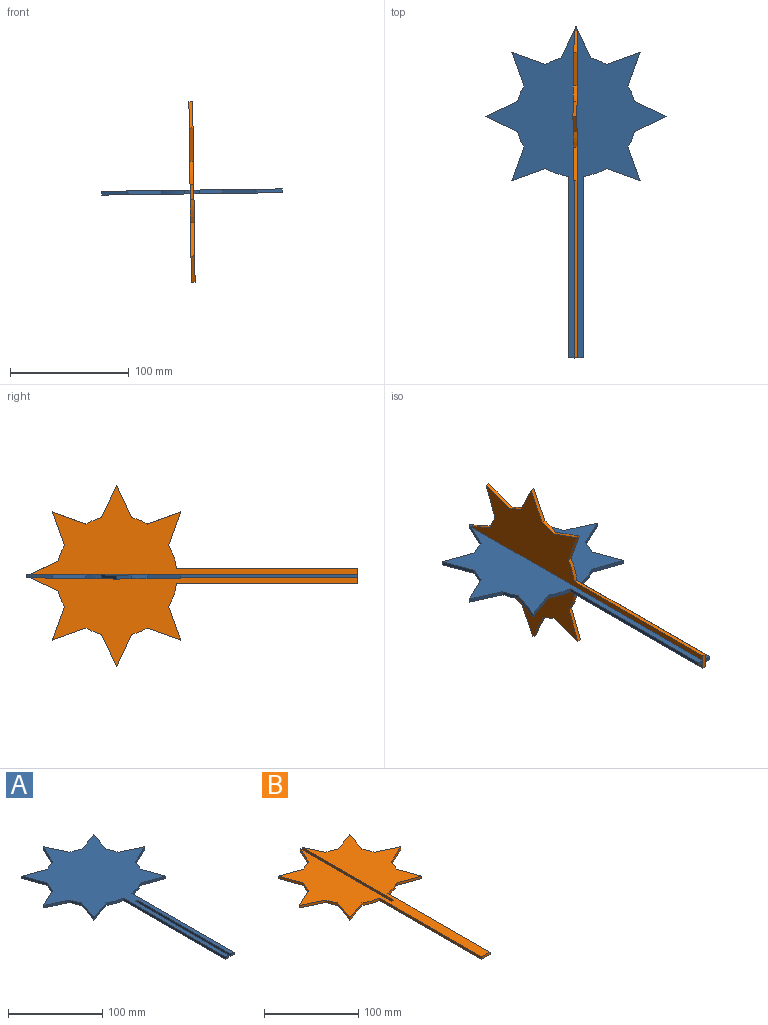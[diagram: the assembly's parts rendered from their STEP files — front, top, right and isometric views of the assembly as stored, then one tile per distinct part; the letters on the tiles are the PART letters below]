
ASSEMBLY  parts=2 mates=1
PART A: 31 faces, bbox 152.4x279.4x3.2 mm
  f0: plane 27.01x12.7mm, normal (0.9,0.43,0), area 94.8mm2, adj f1,f28,f29,f30
  f1: plane 27.01x12.7mm, normal (-0.9,0.43,0), area 94.8mm2, adj f0,f2,f29,f30
  f2: cylinder r=50.8mm len=13.1mm, axis (0,0,-1), area 45.2mm2, adj f1,f3,f29,f30
  f3: plane 28.08x10.12mm, normal (0.34,0.94,0), area 94.8mm2, adj f2,f4,f29,f30
  f4: plane 28.08x10.12mm, normal (-0.94,-0.34,0), area 94.8mm2, adj f3,f5,f29,f30
  f5: cylinder r=50.8mm len=13.1mm, axis (0,0,-1), area 45.2mm2, adj f4,f6,f29,f30
  f6: plane 27.01x12.7mm, normal (-0.43,0.9,0), area 94.8mm2, adj f5,f7,f29,f30
  f7: plane 27.01x12.7mm, normal (-0.43,-0.9,0), area 94.8mm2, adj f6,f8,f29,f30
  f8: cylinder r=50.8mm len=13.1mm, axis (0,0,-1), area 45.2mm2, adj f7,f9,f29,f30
  f9: plane 28.08x10.12mm, normal (-0.94,0.34,0), area 94.8mm2, adj f8,f10,f29,f30
  f10: plane 28.08x10.12mm, normal (0.34,-0.94,0), area 94.8mm2, adj f9,f11,f29,f30
  f11: cylinder r=50.8mm len=19.45mm, axis (0,0,-1), area 65.7mm2, adj f10,f12,f29,f30
  f12: plane 152.8x3.18mm, normal (-1,0,0), area 485.1mm2, adj f11,f13,f29,f30
  f13: plane 4.76x3.18mm, normal (0,-1,0), area 15.1mm2, adj f12,f14,f29,f30
  f14: plane 139.7x3.18mm, normal (1,0,0), area 443.5mm2, adj f13,f15,f29,f30
  f15: plane 3.18x3.18mm, normal (0,-1,0), area 10.1mm2, adj f14,f16,f29,f30
  f16: plane 139.7x3.18mm, normal (-1,0,0), area 443.5mm2, adj f15,f17,f29,f30
  f17: plane 4.76x3.18mm, normal (0,-1,0), area 15.1mm2, adj f16,f18,f29,f30
  f18: plane 152.8x3.18mm, normal (1,0,0), area 485.1mm2, adj f17,f19,f29,f30
  f19: cylinder r=50.8mm len=19.45mm, axis (0,0,-1), area 65.7mm2, adj f18,f20,f29,f30
  f20: plane 28.08x10.12mm, normal (-0.34,-0.94,0), area 94.8mm2, adj f19,f21,f29,f30
  f21: plane 28.08x10.12mm, normal (0.94,0.34,0), area 94.8mm2, adj f20,f22,f29,f30
  f22: cylinder r=50.8mm len=13.1mm, axis (0,0,-1), area 45.2mm2, adj f21,f23,f29,f30
  f23: plane 27.01x12.7mm, normal (0.43,-0.9,0), area 94.8mm2, adj f22,f24,f29,f30
  f24: plane 27.01x12.7mm, normal (0.43,0.9,0), area 94.8mm2, adj f23,f25,f29,f30
  f25: cylinder r=50.8mm len=13.1mm, axis (0,0,-1), area 45.2mm2, adj f24,f26,f29,f30
  f26: plane 28.08x10.12mm, normal (0.94,-0.34,0), area 94.8mm2, adj f25,f27,f29,f30
  f27: plane 28.08x10.12mm, normal (-0.34,0.94,0), area 94.8mm2, adj f26,f28,f29,f30
  f28: cylinder r=50.8mm len=13.1mm, axis (0,0,-1), area 45.2mm2, adj f0,f27,f29,f30
  f29: plane 279.4x152.4mm, normal (0,0,1), area 11810.6mm2, adj f0,f1,f2,f3,f4,f5,f6,f7
  f30: plane 279.4x152.4mm, normal (0,0,-1), area 11810.6mm2, adj f0,f1,f2,f3,f4,f5,f6,f7
PART B: 30 faces, bbox 152.4x276x3.2 mm
  f0: plane 136.32x3.18mm, normal (-1,0,0), area 432.8mm2, adj f1,f27,f28,f29
  f1: plane 3.18x3.18mm, normal (0,1,0), area 10.1mm2, adj f0,f2,f28,f29
  f2: plane 136.32x3.18mm, normal (1,0,0), area 432.8mm2, adj f1,f3,f28,f29
  f3: plane 23.64x11.11mm, normal (-0.9,0.43,0), area 82.9mm2, adj f2,f4,f28,f29
  f4: cylinder r=50.8mm len=13.1mm, axis (0,0,-1), area 45.2mm2, adj f3,f5,f28,f29
  f5: plane 28.08x10.12mm, normal (0.34,0.94,0), area 94.8mm2, adj f4,f6,f28,f29
  f6: plane 28.08x10.12mm, normal (-0.94,-0.34,0), area 94.8mm2, adj f5,f7,f28,f29
  f7: cylinder r=50.8mm len=13.1mm, axis (0,0,-1), area 45.2mm2, adj f6,f8,f28,f29
  f8: plane 27.01x12.7mm, normal (-0.43,0.9,0), area 94.8mm2, adj f7,f9,f28,f29
  f9: plane 27.01x12.7mm, normal (-0.43,-0.9,0), area 94.8mm2, adj f8,f10,f28,f29
  f10: cylinder r=50.8mm len=13.1mm, axis (0,0,-1), area 45.2mm2, adj f9,f11,f28,f29
  f11: plane 28.08x10.12mm, normal (-0.94,0.34,0), area 94.8mm2, adj f10,f12,f28,f29
  f12: plane 28.08x10.12mm, normal (0.34,-0.94,0), area 94.8mm2, adj f11,f13,f28,f29
  f13: cylinder r=50.8mm len=19.45mm, axis (0,0,-1), area 65.7mm2, adj f12,f14,f28,f29
  f14: plane 152.8x3.18mm, normal (-1,0,0), area 485.1mm2, adj f13,f15,f28,f29
  f15: plane 12.7x3.18mm, normal (0,-1,0), area 40.3mm2, adj f14,f16,f28,f29
  f16: plane 152.8x3.18mm, normal (1,0,0), area 485.1mm2, adj f15,f17,f28,f29
  f17: cylinder r=50.8mm len=19.45mm, axis (0,0,-1), area 65.7mm2, adj f16,f18,f28,f29
  f18: plane 28.08x10.12mm, normal (-0.34,-0.94,0), area 94.8mm2, adj f17,f19,f28,f29
  f19: plane 28.08x10.12mm, normal (0.94,0.34,0), area 94.8mm2, adj f18,f20,f28,f29
  f20: cylinder r=50.8mm len=13.1mm, axis (0,0,-1), area 45.2mm2, adj f19,f21,f28,f29
  f21: plane 27.01x12.7mm, normal (0.43,-0.9,0), area 94.8mm2, adj f20,f22,f28,f29
  f22: plane 27.01x12.7mm, normal (0.43,0.9,0), area 94.8mm2, adj f21,f23,f28,f29
  f23: cylinder r=50.8mm len=13.1mm, axis (0,0,-1), area 45.2mm2, adj f22,f24,f28,f29
  f24: plane 28.08x10.12mm, normal (0.94,-0.34,0), area 94.8mm2, adj f23,f25,f28,f29
  f25: plane 28.08x10.12mm, normal (-0.34,0.94,0), area 94.8mm2, adj f24,f26,f28,f29
  f26: cylinder r=50.8mm len=13.1mm, axis (0,0,-1), area 45.2mm2, adj f25,f27,f28,f29
  f27: plane 23.64x11.11mm, normal (0.9,0.43,0), area 82.9mm2, adj f0,f26,f28,f29
  f28: plane 276.02x152.4mm, normal (0,0,1), area 11815.9mm2, adj f0,f1,f2,f3,f4,f5,f6,f7
  f29: plane 276.02x152.4mm, normal (0,0,-1), area 11815.9mm2, adj f0,f1,f2,f3,f4,f5,f6,f7
PLACE A rot(axis=(0,1,0),179.2deg) t=(226.25,-3.06,40.87)mm
PLACE B rot(axis=(0,1,0),89.2deg) t=(224.68,-3.13,39.26)mm
MATE slider A.f15 <-> B.f1  axis (0,-1,0) through (226.27,35.04,39.28)mm
